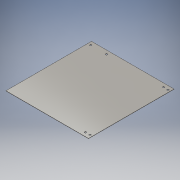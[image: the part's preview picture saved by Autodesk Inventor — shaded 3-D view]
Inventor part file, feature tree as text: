
AUTODESK INVENTOR PART (.ipt)
format: ipt  version: 2016 (Build 200138000, 138)  size: 157,696 bytes
history: native  units: mm
features: hole x2, other x2, sketch x2, sheet_metal_op x1
ambient origin geometry x8: Origin, YZ Plane, XZ Plane, XY Plane, X Axis, Y Axis, Z Axis, Center Point
bodies: Solid1 (feature_tree)
feature tree (7):
  sheet_metal_op  "Face1"
  hole  "Hole3"  [1 undecoded]
  hole  "Hole4"  [1 undecoded]
  other  "Plate1"
  sketch  "Sketch7"  dims[d2=550.0mm d3=570.0mm]
  sketch  "Sketch8"  dims[d4=1.6mm d57=60.0mm d58=12.0mm d59=12.0mm d60=15.0mm d61=15.0mm d62=25.0mm d63=25.0mm d64=12.0mm d65=12.0mm d66=25.0mm d67=25.0mm d68=12.0mm d69=6.0mm d70=4.0mm d71=2.0mm d72=90.0deg d73=1.6mm d74=20.594885mm d75=15.0mm d76=15.0mm d79=145.0mm d80=12.0mm d81=25.0mm d82=20.0mm d83=12.0mm d84=20.0mm d85=12.0mm d86=6.0mm d87=4.0mm d88=2.0mm d89=90.0deg d90=1.6mm d91=20.594885mm]
  other  "Definition1"
note: 2 required parameter values undecoded (feature->parameter linkage not recoverable at this tier; creation-order binding heuristic only, values carry confidence <= 0.55)
